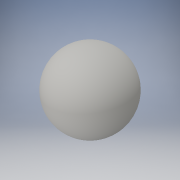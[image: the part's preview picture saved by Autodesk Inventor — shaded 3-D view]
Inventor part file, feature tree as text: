
AUTODESK INVENTOR PART (.ipt)
format: ipt  version: 2016 (Build 200138000, 138)  size: 112,640 bytes
history: native  units: in
note: dims shown in document units (in); Inventor stores cm internally (conversion verified against a paired STEP export)
features: revolve x1, sketch x1
ambient origin geometry x8: Origin, YZ Plane, XZ Plane, XY Plane, X Axis, Y Axis, Z Axis, Center Point
bodies: Solid1 (feature_tree)
feature tree (2):
  revolve  "Revolution1"  Angle=90.0deg
  sketch  "Sketch1"  dims[d0=0.73in d1=90.0deg]
